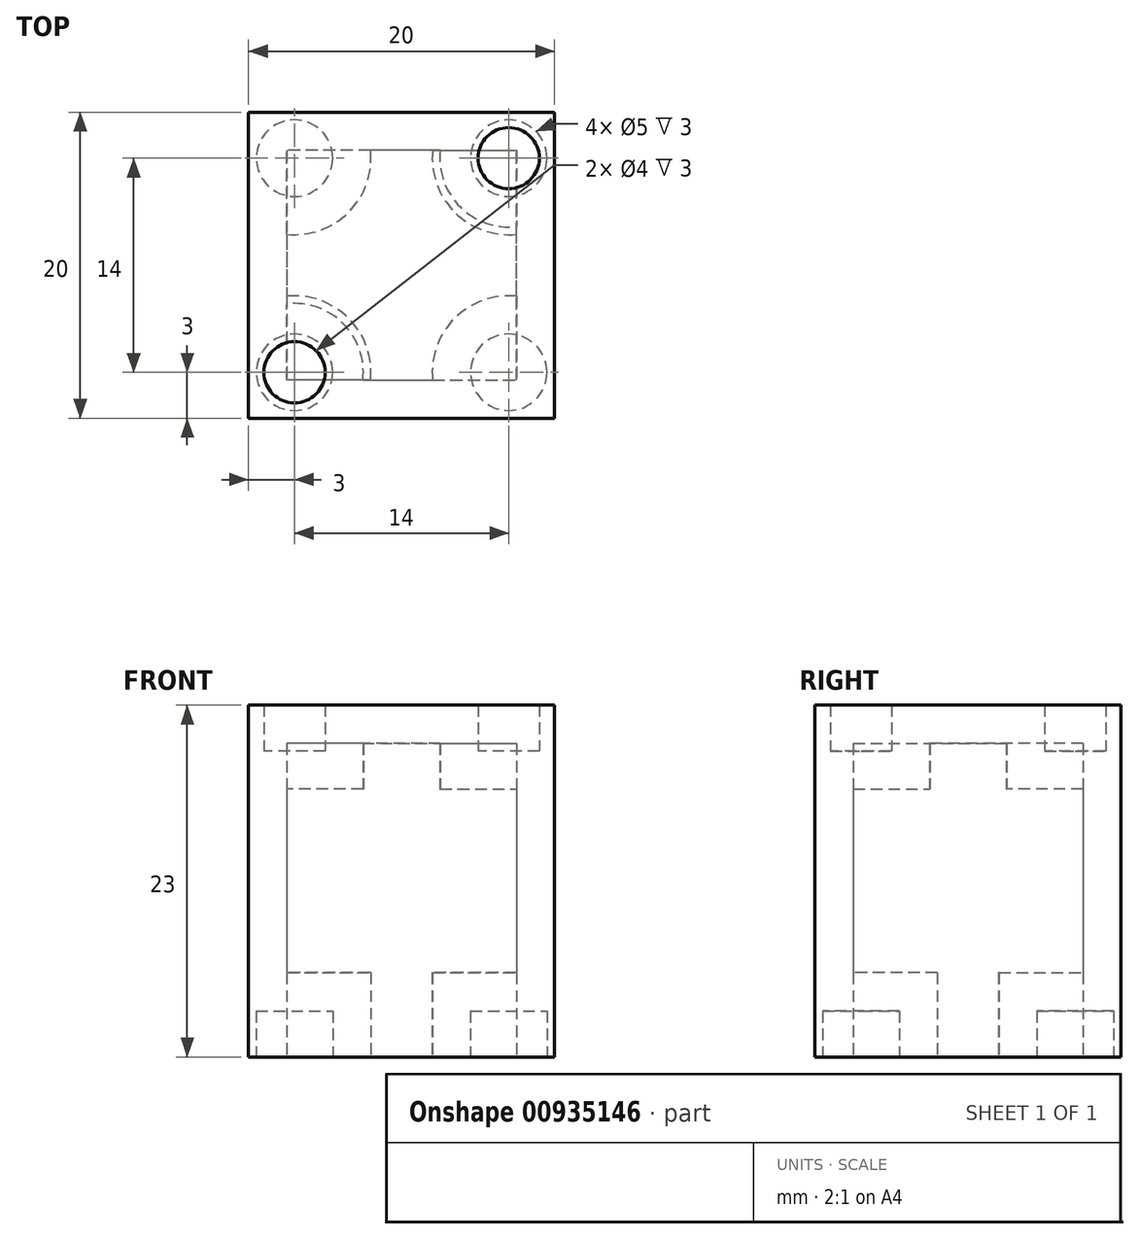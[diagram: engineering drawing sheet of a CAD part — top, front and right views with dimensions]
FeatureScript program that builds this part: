
annotation { "Feature Type Name" : "Feature", "Feature Type Description" : "" }
export const myFeature = defineFeature(function(context is Context, id is Id, definition is map)
    precondition{}
    {
        {
            var Q0;
            Q0=qCreatedBy(makeId("Top.planeOp"),FACE);
            var sketch = newSketch(context, id + "F0", { "sketchPlane" : qUnion([Q0])});
            skLineSegment(sketch, "E0", {"start": v(-10, 10) * mm, "end": v(-10, -10) * mm});
            skLineSegment(sketch, "E1", {"start": v(-10, -10) * mm, "end": v(10, -10) * mm});
            skLineSegment(sketch, "E2", {"start": v(10, -10) * mm, "end": v(10, 10) * mm});
            skLineSegment(sketch, "E3", {"start": v(10, 10) * mm, "end": v(-10, 10) * mm});
            skPoint(sketch, "E4", {"position": v(0, 10) * mm});
            skPoint(sketch, "E5", {"position": v(10, 0) * mm});
            skSolve(sketch);
        }
        {
            var Q0;
            Q0=makeQuery(id+"F0.imprint","IMPRINT",FACE,{"disambiguationData":[TD([[makeQuery(id+"F0.imprint","IMPRINT",EDGE,{"derivedFrom":sQuery(id+"F0.wireOp",EDGE,"E0")}),1.0]])]});
            extrude(context, id + "F1", {"entities" : qUnion([Q0]), "depth" : 20 * mm, "offsetDistance" : 25 * mm});
        }
        {
            var Q0;
            Q0=makeQuery(id+"F1.opExtrude","CAP_FACE",FACE,{"disambiguationData":[OSD([sQuery(id+"F0.wireOp",EDGE,"E0"),sQuery(id+"F0.wireOp",EDGE,"E1"),sQuery(id+"F0.wireOp",EDGE,"E2"),sQuery(id+"F0.wireOp",EDGE,"E3")])],"isStart":false});
            var sketch = newSketch(context, id + "F2", { "sketchPlane" : qUnion([Q0])});
            skCircle(sketch, "E6", {"center": v(-5.3, 5.3) * mm, "radius": 2 * mm});
            skCircle(sketch, "E7", {"center": v(0, 0) * mm, "radius": 7.5 * mm, "construction": true});
            skPoint(sketch, "E7.centerSnap0", {"position": v(10, 0) * mm});
            skPoint(sketch, "E7.centerSnap1", {"position": v(0, 10) * mm});
            skLineSegment(sketch, "E8", {"start": v(-5.3, 5.3) * mm, "end": v(-10, 10) * mm, "construction": true});
            skCircle(sketch, "E9.1.0", {"center": v(-5.3, -5.3) * mm, "radius": 2 * mm});
            skCircle(sketch, "E9.2.0", {"center": v(5.3, -5.3) * mm, "radius": 2 * mm});
            skCircle(sketch, "E9.3.0", {"center": v(5.3, 5.3) * mm, "radius": 2 * mm});
            skSolve(sketch);
        }
        {
            var Q0;
            Q0=makeQuery(id+"F1.opExtrude","CAP_FACE",FACE,{"disambiguationData":[OSD([sQuery(id+"F0.wireOp",EDGE,"E0"),sQuery(id+"F0.wireOp",EDGE,"E1"),sQuery(id+"F0.wireOp",EDGE,"E2"),sQuery(id+"F0.wireOp",EDGE,"E3")])],"isStart":false});
            var sketch = newSketch(context, id + "F3", { "sketchPlane" : qUnion([Q0])});
            skCircle(sketch, "E10", {"center": v(-7, 7) * mm, "radius": 2 * mm});
            skCircle(sketch, "E11.MirrorC", {"center": v(7, 7) * mm, "radius": 2 * mm});
            skCircle(sketch, "E12.MirrorC", {"center": v(-7, -7) * mm, "radius": 2 * mm});
            skCircle(sketch, "E13.MirrorC", {"center": v(7, -7) * mm, "radius": 2 * mm});
            skSolve(sketch);
        }
        {
            var Q0;
            Q0=makeQuery(id+"F3.imprint","IMPRINT",FACE,{"disambiguationData":[TD([[makeQuery(id+"F3.imprint","IMPRINT",EDGE,{"derivedFrom":sQuery(id+"F3.wireOp",EDGE,"E12.MirrorC")}),-1.0]])]});
            var Q1;
            Q1=makeQuery(id+"F3.imprint","IMPRINT",FACE,{"disambiguationData":[TD([[makeQuery(id+"F3.imprint","IMPRINT",EDGE,{"derivedFrom":sQuery(id+"F3.wireOp",EDGE,"E11.MirrorC")}),-1.0]])]});
            var Q2;
            Q2=makeQuery(id+"F3.imprint","IMPRINT",FACE,{"disambiguationData":[TD([[makeQuery(id+"F3.imprint","IMPRINT",EDGE,{"derivedFrom":sQuery(id+"F3.wireOp",EDGE,"E13.MirrorC")}),1.0]])]});
            var Q3;
            Q3=makeQuery(id+"F3.imprint","IMPRINT",FACE,{"disambiguationData":[TD([[makeQuery(id+"F3.imprint","IMPRINT",EDGE,{"derivedFrom":sQuery(id+"F3.wireOp",EDGE,"E10")}),1.0]])]});
            extrude(context, id + "F4", {"entities" : qUnion([Q0, Q1, Q2, Q3]), "operationType" : NewBodyOperationType.ADD, "depth" : 3 * mm, "offsetDistance" : 25 * mm});
        }
        {
            var Q0;
            Q0=makeQuery(id+"F1.opExtrude","CAP_FACE",FACE,{"disambiguationData":[OSD([sQuery(id+"F0.wireOp",EDGE,"E0"),sQuery(id+"F0.wireOp",EDGE,"E1"),sQuery(id+"F0.wireOp",EDGE,"E2"),sQuery(id+"F0.wireOp",EDGE,"E3")])],"isStart":true});
            var sketch = newSketch(context, id + "F5", { "sketchPlane" : qUnion([Q0])});
            skCircle(sketch, "E14", {"center": v(-7, 7) * mm, "radius": 2.5 * mm});
            skCircle(sketch, "E15.MirrorC", {"center": v(7, 7) * mm, "radius": 2.5 * mm});
            skCircle(sketch, "E16.MirrorC", {"center": v(-7, -7) * mm, "radius": 2.5 * mm});
            skCircle(sketch, "E17.MirrorC", {"center": v(7, -7) * mm, "radius": 2.5 * mm});
            skSolve(sketch);
        }
        {
            var Q0;
            Q0 = qSketchRegion(id + "F5", true);
            extrude(context, id + "F6", {"entities" : qUnion([Q0]), "operationType" : NewBodyOperationType.REMOVE, "oppositeDirection" : true, "depth" : 3 * mm, "offsetDistance" : 25 * mm});
        }
        {
            var Q0;
            Q0=makeQuery(id+"F1.opExtrude","CAP_FACE",FACE,{"disambiguationData":[OSD([sQuery(id+"F0.wireOp",EDGE,"E0"),sQuery(id+"F0.wireOp",EDGE,"E1"),sQuery(id+"F0.wireOp",EDGE,"E2"),sQuery(id+"F0.wireOp",EDGE,"E3")])],"isStart":true});
            shell(context, id + "F7", {"entities" : qUnion([Q0]), "thickness" : 2.5 * mm});
        }
    });
